# Revit family: MBA_Штора_Противопожарная_FireTechnics_Горизонтальная
name_source: partatom
category: Двери
revit_build: Autodesk Revit 2016 (Build: 20160314_0715(x64)
units: mm (PartAtom-declared; Revit-internal decimal feet)

## family parameters
Всегда вертикально = Нет
На основе рабочей плоскости = Да
Общий = Нет
При загрузке вырезать с полостями = Нет
Точка расчета площади = Нет

## types (2) — shared parameters
ADSK_URL страницы изделия = https://mva-rolltor.ru
ADSK_Единица измерения = шт.
ADSK_Завод-изготовитель = МВА
ADSK_Обозначение = ТУ 5284-001-16123348-2020
ADSK_Размер_Высота = 3530 мм
ADSK_Размер_Ширина = 3160 мм
URL = https://mva-rolltor.ru
h1 = 290 мм
h2 = 240 мм
Аналитическая конструкция = <Нет>
Высота = 3000 мм
Высота верхнего короба = 200 мм
Высота направляющей = 60 мм
Высота нижнего короба = 200 мм
Изготовитель = МВА
Материал корпуса = Сталь_оцинкованная_листовая МВА
Материал нижнего корпуса = Сталь_оцинкованная_листовая_1,5мм_МВА
Материал полотна = Firetex™ 1100
Описание = Горизонтальные автоматические противопожарные шторы служат для предотвращения вертикального распространения огня и дыма между этажами и из одной части здания в другую.
Тип конструкций = Штора противопожарная
Толщина полотна = 3 мм
Функция = Внутренние слои
Ширина = 3000 мм
Ширина верхнего короба = 220 мм
Ширина направляющей = 80 мм
Ширина нижнего короба = 220 мм
zero-valued in all types: Отметка по умолчанию

## per-type parameters (varying)
| type | ADSK_Масса_Текст | ADSK_Наименование | ADSK_Наименование краткое | ADSK_Предел огнестойкости | Огнестойкость |
| EI60 (без орошения водой) | Вес ткани: 2500 г/м² | Противопожарная штора FireTechnics-H EI-60 ("Горизонтальная") без орошения водой | Противопожарная штора FireTechnics-H EI-60 ("Горизонтальная") | EI60 | EI60 |
| EI180 (при орошении водой) | Вес ткани: 660 г/м² | Противопожарная штора FireTechnics-H EI-180 ("Горизонтальная") при орошении водой | Противопожарная штора FireTechnics-H EI-180 ("Горизонтальная") | EI180 | EI180 |
